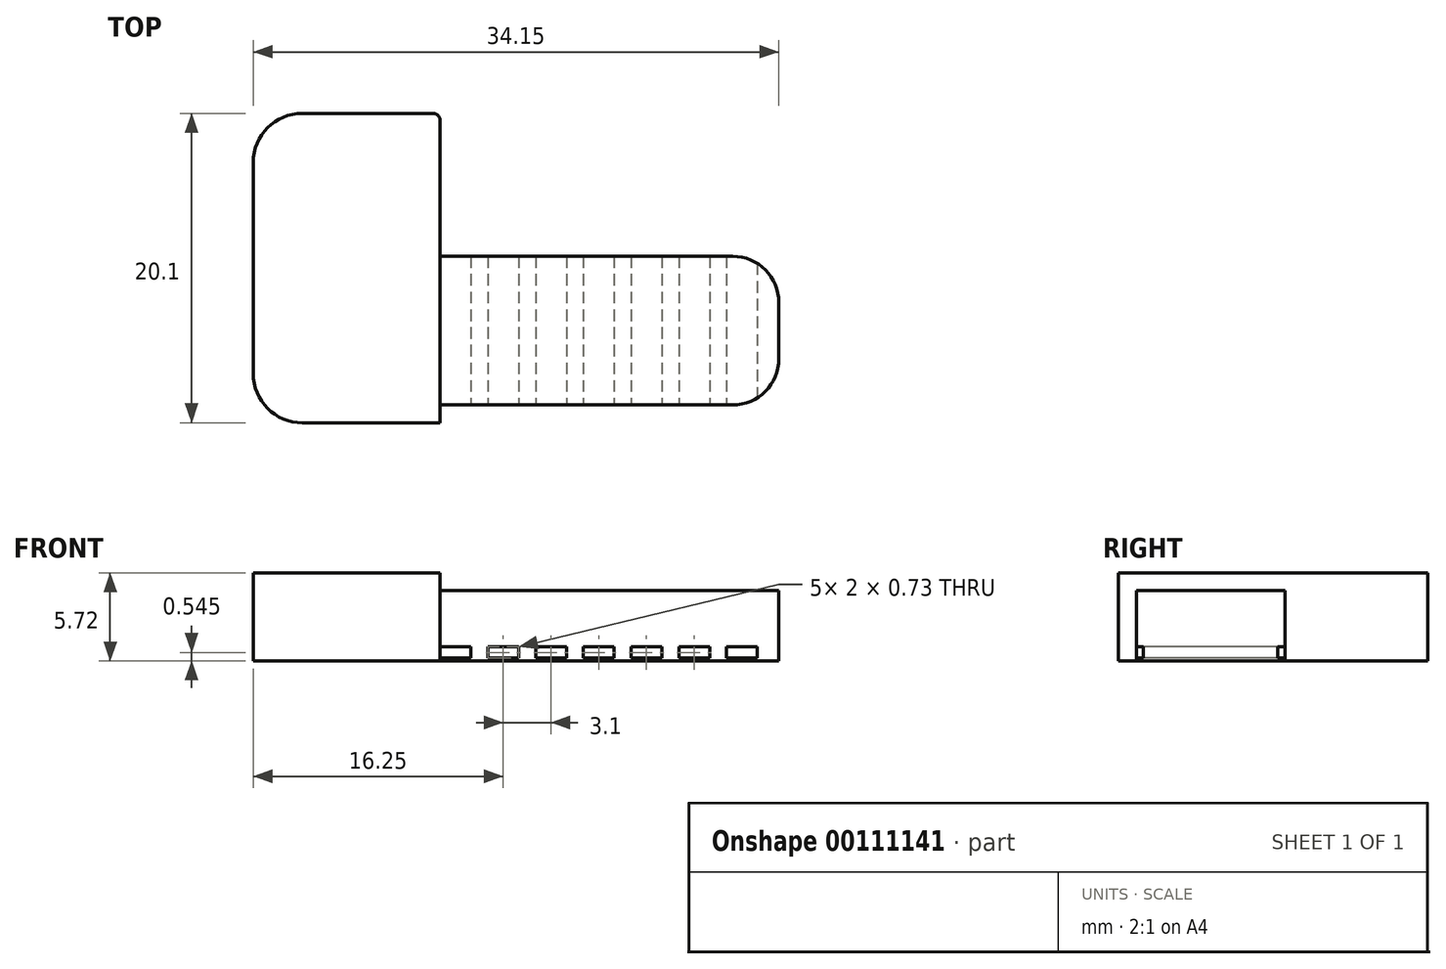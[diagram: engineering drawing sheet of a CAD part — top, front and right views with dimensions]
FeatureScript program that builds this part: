
annotation { "Feature Type Name" : "Feature", "Feature Type Description" : "" }
export const myFeature = defineFeature(function(context is Context, id is Id, definition is map)
    precondition{}
    {
        {
            assignVariable(context, id + "F0", {"name" : "metalWall", "anyValue" : 1.16});
        }
        {
            var Q0;
            Q0=qCreatedBy(makeId("Top.planeOp"),FACE);
            var sketch = newSketch(context, id + "F1", { "sketchPlane" : qUnion([Q0])});
            skLineSegment(sketch, "E0", {"start": v(3.2, 0) * mm, "end": v(12.15, 0) * mm});
            skLineSegment(sketch, "E1", {"start": v(34.15, 0) * mm, "end": v(34.15, 1.16) * mm, "construction": true});
            skLineSegment(sketch, "E2", {"start": v(31.15, 10.8) * mm, "end": v(12.15, 10.8) * mm});
            skLineSegment(sketch, "E3", {"start": v(12.15, 10.8) * mm, "end": v(12.15, 19.6) * mm});
            skLineSegment(sketch, "E4", {"start": v(11.65, 20.1) * mm, "end": v(3.2, 20.1) * mm});
            skLineSegment(sketch, "E5", {"start": v(0, 16.9) * mm, "end": v(0, 3.2) * mm});
            skPoint(sketch, "E6.visualSharp", {"position": v(0, 20.1) * mm});
            skArc(sketch, "E6.filletArc", {"start": v(3.2, 20.1) * mm, "mid": v(0.94, 19.16) * mm, "end": v(0, 16.9) * mm});
            skPoint(sketch, "E7.visualSharp", {"position": v(0, 0) * mm});
            skArc(sketch, "E7.filletArc", {"start": v(0, 3.2) * mm, "mid": v(0.94, 0.94) * mm, "end": v(3.2, 0) * mm});
            skLineSegment(sketch, "E8", {"start": v(31.15, 1.16) * mm, "end": v(12.15, 1.16) * mm});
            skLineSegment(sketch, "E9", {"start": v(12.15, 1.16) * mm, "end": v(12.15, 0) * mm});
            skLineSegment(sketch, "E10", {"start": v(12.15, 11.97) * mm, "end": v(34.15, 11.97) * mm, "construction": true});
            skLineSegment(sketch, "E11", {"start": v(34.15, 11.97) * mm, "end": v(34.15, 10.8) * mm, "construction": true});
            skLineSegment(sketch, "E12", {"start": v(12.15, 0) * mm, "end": v(34.15, 0) * mm, "construction": true});
            skLineSegment(sketch, "E13", {"start": v(34.15, 4.16) * mm, "end": v(34.15, 7.8) * mm});
            skPoint(sketch, "E14.visualSharp", {"position": v(12.15, 20.1) * mm});
            skArc(sketch, "E14.filletArc", {"start": v(12.15, 19.6) * mm, "mid": v(12, 19.95) * mm, "end": v(11.65, 20.1) * mm});
            skLineSegment(sketch, "E15", {"start": v(12.15, 10.8) * mm, "end": v(12.15, 1.16) * mm});
            skPoint(sketch, "E16.visualSharp", {"position": v(34.15, 10.8) * mm});
            skArc(sketch, "E16.filletArc", {"start": v(34.15, 7.8) * mm, "mid": v(33.27, 9.93) * mm, "end": v(31.15, 10.8) * mm});
            skPoint(sketch, "E17.visualSharp", {"position": v(34.15, 1.16) * mm});
            skArc(sketch, "E17.filletArc", {"start": v(31.15, 1.16) * mm, "mid": v(33.27, 2.04) * mm, "end": v(34.15, 4.16) * mm});
            skLineSegment(sketch, "E18", {"start": v(34.15, 1.16) * mm, "end": v(34.15, 4.16) * mm, "construction": true});
            skLineSegment(sketch, "E19", {"start": v(34.15, 1.16) * mm, "end": v(31.15, 1.16) * mm, "construction": true});
            skLineSegment(sketch, "E20", {"start": v(34.15, 7.8) * mm, "end": v(34.15, 10.8) * mm, "construction": true});
            skSolve(sketch);
        }
        {
            var Q0;
            Q0=makeQuery(id+"F1.imprint","IMPRINT",FACE,{"disambiguationData":[TD([[makeQuery(id+"F1.imprint","IMPRINT",EDGE,{"derivedFrom":sQuery(id+"F1.wireOp",EDGE,"E0")}),1.0]])]});
            extrude(context, id + "F2", {"entities" : qUnion([Q0]), "depth" : (6.3 - (getVariable(context, 'metalWall') / 2)) * mm, "offsetDistance" : 25 * mm});
        }
        {
            var Q0;
            Q0=makeQuery(id+"F1.imprint","IMPRINT",FACE,{"disambiguationData":[TD([[makeQuery(id+"F1.imprint","IMPRINT",EDGE,{"derivedFrom":sQuery(id+"F1.wireOp",EDGE,"E2")}),1.0]])]});
            extrude(context, id + "F3", {"entities" : qUnion([Q0]), "operationType" : NewBodyOperationType.ADD, "depth" : (6.3 - (getVariable(context, 'metalWall') + getVariable(context, 'metalWall') / 2)) * mm, "offsetDistance" : 25 * mm});
        }
        {
            var Q0;
            Q0=makeQuery(id+"F3.opExtrude","SWEPT_FACE",FACE,{"disambiguationData":[OSD([sQuery(id+"F1.wireOp",EDGE,"E8")])]});
            var sketch = newSketch(context, id + "F4", { "sketchPlane" : qUnion([Q0])});
            skLineSegment(sketch, "E21", {"start": v(12.15, 0.18) * mm, "end": v(14.15, 0.18) * mm});
            skLineSegment(sketch, "E22", {"start": v(14.15, 0.18) * mm, "end": v(14.15, 0.91) * mm});
            skLineSegment(sketch, "E23", {"start": v(14.15, 0.91) * mm, "end": v(12.15, 0.9) * mm});
            skLineSegment(sketch, "E24", {"start": v(12.15, 0.9) * mm, "end": v(12.15, 0.18) * mm});
            skLineSegment(sketch, "E25.1.0.0", {"start": v(15.25, 0.9) * mm, "end": v(15.25, 0.18) * mm});
            skLineSegment(sketch, "E25.1.0.1", {"start": v(17.25, 0.9) * mm, "end": v(15.25, 0.9) * mm});
            skLineSegment(sketch, "E25.1.0.2", {"start": v(17.25, 0.18) * mm, "end": v(17.25, 0.91) * mm});
            skLineSegment(sketch, "E25.1.0.3", {"start": v(15.25, 0.18) * mm, "end": v(17.25, 0.18) * mm});
            skLineSegment(sketch, "E25.2.0.0", {"start": v(18.35, 0.9) * mm, "end": v(18.35, 0.18) * mm});
            skLineSegment(sketch, "E25.2.0.1", {"start": v(20.35, 0.9) * mm, "end": v(18.35, 0.9) * mm});
            skLineSegment(sketch, "E25.2.0.2", {"start": v(20.35, 0.18) * mm, "end": v(20.35, 0.91) * mm});
            skLineSegment(sketch, "E25.2.0.3", {"start": v(18.35, 0.18) * mm, "end": v(20.35, 0.18) * mm});
            skLineSegment(sketch, "E25.3.0.0", {"start": v(21.45, 0.9) * mm, "end": v(21.45, 0.18) * mm});
            skLineSegment(sketch, "E25.3.0.1", {"start": v(23.45, 0.9) * mm, "end": v(21.45, 0.9) * mm});
            skLineSegment(sketch, "E25.3.0.2", {"start": v(23.45, 0.18) * mm, "end": v(23.45, 0.91) * mm});
            skLineSegment(sketch, "E25.3.0.3", {"start": v(21.45, 0.18) * mm, "end": v(23.45, 0.18) * mm});
            skLineSegment(sketch, "E25.4.0.0", {"start": v(24.55, 0.9) * mm, "end": v(24.55, 0.18) * mm});
            skLineSegment(sketch, "E25.4.0.1", {"start": v(26.55, 0.9) * mm, "end": v(24.55, 0.9) * mm});
            skLineSegment(sketch, "E25.4.0.2", {"start": v(26.55, 0.18) * mm, "end": v(26.55, 0.91) * mm});
            skLineSegment(sketch, "E25.4.0.3", {"start": v(24.55, 0.18) * mm, "end": v(26.55, 0.18) * mm});
            skLineSegment(sketch, "E25.direction1", {"start": v(12.15, 0.18) * mm, "end": v(15.25, 0.18) * mm, "construction": true});
            skLineSegment(sketch, "E26.0.5.0", {"start": v(27.65, 0.9) * mm, "end": v(27.65, 0.18) * mm});
            skLineSegment(sketch, "E26.3.5.0", {"start": v(29.65, 0.91) * mm, "end": v(27.65, 0.9) * mm});
            skLineSegment(sketch, "E26.6.5.0", {"start": v(29.65, 0.18) * mm, "end": v(29.65, 0.91) * mm});
            skLineSegment(sketch, "E26.9.5.0", {"start": v(27.65, 0.18) * mm, "end": v(29.65, 0.18) * mm});
            skLineSegment(sketch, "E27.0.6.0", {"start": v(30.75, 0.9) * mm, "end": v(30.75, 0.18) * mm});
            skLineSegment(sketch, "E27.3.6.0", {"start": v(32.75, 0.9) * mm, "end": v(30.75, 0.9) * mm});
            skLineSegment(sketch, "E27.6.6.0", {"start": v(32.75, 0.18) * mm, "end": v(32.75, 0.91) * mm});
            skLineSegment(sketch, "E27.9.6.0", {"start": v(30.75, 0.18) * mm, "end": v(32.75, 0.18) * mm});
            skSolve(sketch);
        }
        {
            var Q0;
            Q0 = qSketchRegion(id + "F4", true);
            extrude(context, id + "F5", {"entities" : qUnion([Q0]), "operationType" : NewBodyOperationType.REMOVE, "endBound" : BoundingType.THROUGH_ALL, "oppositeDirection" : true, "depth" : 25 * mm, "offsetDistance" : 25 * mm});
        }
    });
